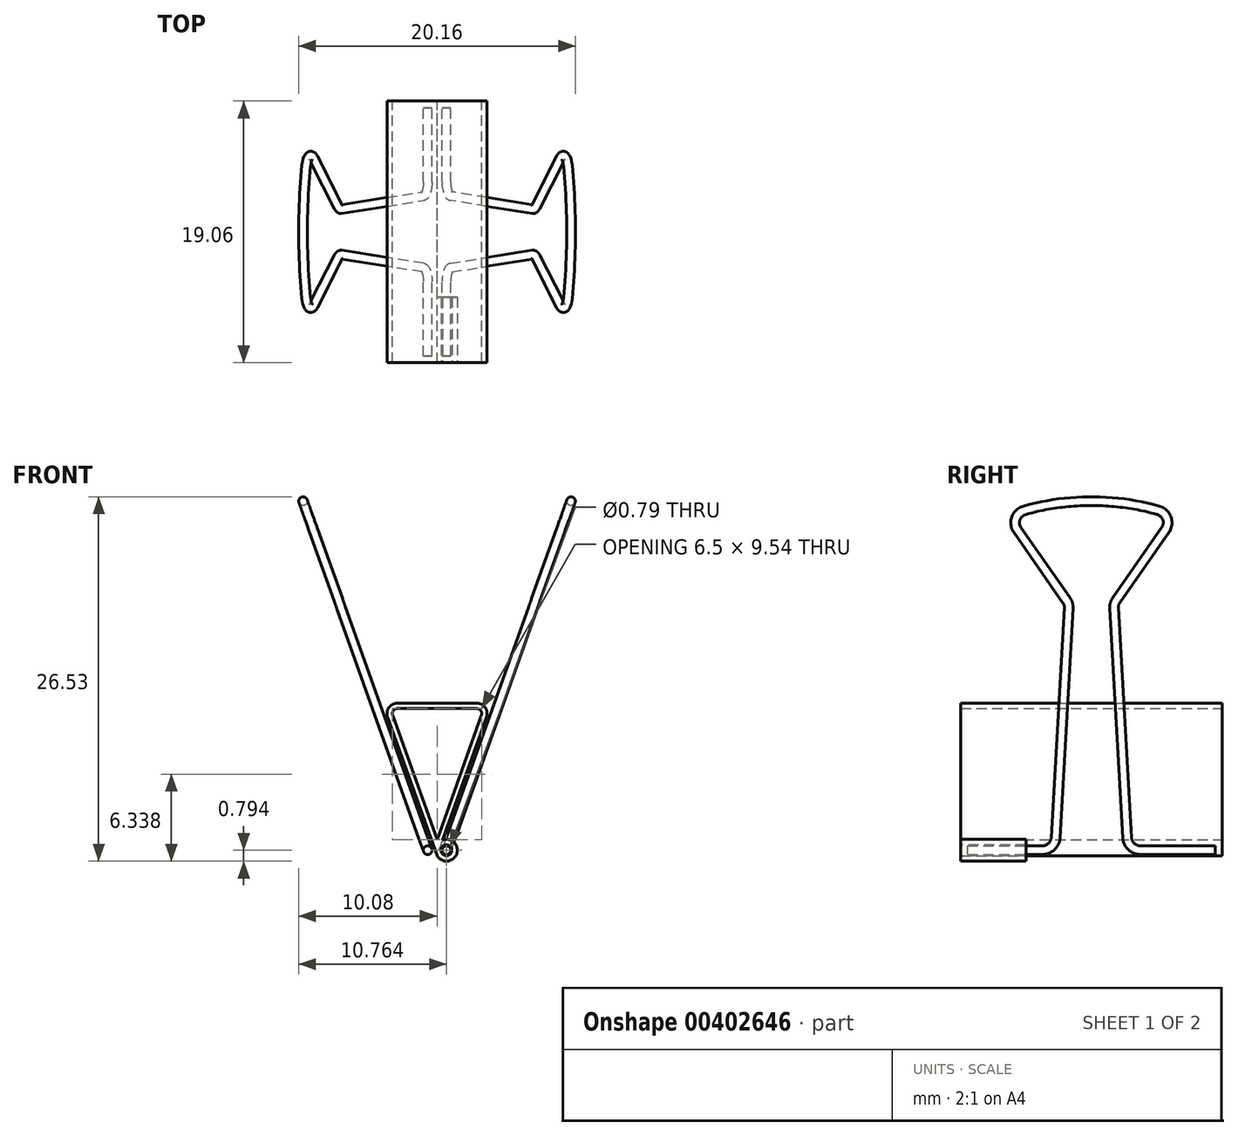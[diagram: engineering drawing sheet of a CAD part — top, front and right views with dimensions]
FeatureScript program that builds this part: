
annotation { "Feature Type Name" : "Feature", "Feature Type Description" : "" }
export const myFeature = defineFeature(function(context is Context, id is Id, definition is map)
    precondition{}
    {
        {
            var Q0;
            Q0=qCreatedBy(makeId("Front.planeOp"),FACE);
            var sketch = newSketch(context, id + "F0", { "sketchPlane" : qUnion([Q0])});
            skLineSegment(sketch, "E0", {"start": v(0, 0) * mm, "end": v(-3.97, 11.11) * mm});
            skLineSegment(sketch, "E1", {"start": v(-3.97, 11.11) * mm, "end": v(3.97, 11.11) * mm});
            skLineSegment(sketch, "E2", {"start": v(3.97, 11.11) * mm, "end": v(0, 0) * mm});
            skSolve(sketch);
        }
        {
            var Q0;
            Q0 = qSketchRegion(id + "F0", true);
            extrude(context, id + "F1", {"entities" : qUnion([Q0]), "depth" : 19.05 * mm, "symmetric" : true});
        }
        {
            var Q0;
            Q0=makeQuery(id+"F1.opExtrude","SWEPT_EDGE",EDGE,{"disambiguationData":[OSD([sQuery(id+"F0.wireOp",EDGE,"E1"),sQuery(id+"F0.wireOp",EDGE,"E2")])]});
            var Q1;
            Q1=makeQuery(id+"F1.opExtrude","SWEPT_EDGE",EDGE,{"disambiguationData":[OSD([sQuery(id+"F0.wireOp",EDGE,"E0"),sQuery(id+"F0.wireOp",EDGE,"E1")])]});
            fillet(context, id + "F2", {"entities" : qUnion([Q0, Q1]), "radius" : 0.76 * mm, "tangentPropagation" : true, "allowEdgeOverflow" : false});
        }
        {
            var Q0;
            Q0=makeQuery(id+"F1.opExtrude","CAP_FACE",FACE,{"disambiguationData":[OSD([sQuery(id+"F0.wireOp",EDGE,"E0"),sQuery(id+"F0.wireOp",EDGE,"E1"),sQuery(id+"F0.wireOp",EDGE,"E2")])],"isStart":false});
            shell(context, id + "F3", {"entities" : qUnion([Q0]), "thickness" : 0.4 * mm});
        }
        {
            var Q0;
            Q0=makeQuery(id+"F1.opExtrude","CAP_FACE",FACE,{"disambiguationData":[OSD([sQuery(id+"F0.wireOp",EDGE,"E0"),sQuery(id+"F0.wireOp",EDGE,"E1"),sQuery(id+"F0.wireOp",EDGE,"E2")])],"isStart":true});
            var sketch = newSketch(context, id + "F4", { "sketchPlane" : qUnion([Q0])});
            skLineSegment(sketch, "E3.0", {"start": v(2.89, 10.72) * mm, "end": v(-2.89, 10.72) * mm});
            skArc(sketch, "E4.0", {"start": v(-2.89, 10.72) * mm, "mid": v(-3.19, 10.56) * mm, "end": v(-3.23, 10.23) * mm});
            skLineSegment(sketch, "E5.0", {"start": v(-3.23, 10.23) * mm, "end": v(0, 1.18) * mm});
            skLineSegment(sketch, "E6.0", {"start": v(0, 1.18) * mm, "end": v(3.23, 10.23) * mm});
            skArc(sketch, "E7.0", {"start": v(3.23, 10.23) * mm, "mid": v(3.19, 10.56) * mm, "end": v(2.89, 10.72) * mm});
            skSolve(sketch);
        }
        {
            var Q0;
            Q0 = qSketchRegion(id + "F4", true);
            extrude(context, id + "F5", {"entities" : qUnion([Q0]), "operationType" : NewBodyOperationType.REMOVE, "endBound" : BoundingType.THROUGH_ALL, "oppositeDirection" : true, "depth" : 25.4 * mm});
        }
        {
            var Q0;
            Q0=makeQuery(id+"F1.opExtrude","CAP_FACE",FACE,{"disambiguationData":[OSD([sQuery(id+"F0.wireOp",EDGE,"E0"),sQuery(id+"F0.wireOp",EDGE,"E1"),sQuery(id+"F0.wireOp",EDGE,"E2")])],"isStart":false});
            var sketch = newSketch(context, id + "F6", { "sketchPlane" : qUnion([Q0])});
            skArc(sketch, "E8", {"start": v(0, 0) * mm, "mid": v(1.43, 0.14) * mm, "end": v(0.41, 1.15) * mm});
            skLineSegment(sketch, "E9", {"start": v(0.41, 1.15) * mm, "end": v(0, 0) * mm});
            skSolve(sketch);
        }
        {
            var Q0;
            Q0 = qSketchRegion(id + "F6", true);
            var Q1;
            Q1=makeQuery(id+"F1.opExtrude","CAP_FACE",FACE,{"disambiguationData":[OSD([sQuery(id+"F0.wireOp",EDGE,"E0"),sQuery(id+"F0.wireOp",EDGE,"E1"),sQuery(id+"F0.wireOp",EDGE,"E2")])],"isStart":true});
            extrude(context, id + "F7", {"entities" : qUnion([Q0]), "operationType" : NewBodyOperationType.ADD, "oppositeDirection" : true, "endBoundEntityFace" : qUnion([Q1]), "depth" : 4.76 * mm});
        }
        {
            var Q0;
            Q0=makeQuery(id+"F7.boolean.opBoolean","MERGE",FACE,{"derivedFrom":[makeQuery(id+"F1.opExtrude","CAP_FACE",FACE,{"disambiguationData":[OSD([sQuery(id+"F0.wireOp",EDGE,"E0"),sQuery(id+"F0.wireOp",EDGE,"E1"),sQuery(id+"F0.wireOp",EDGE,"E2")])],"isStart":false}),makeQuery(id+"F7.opExtrude","CAP_FACE",FACE,{"disambiguationData":[OSD([sQuery(id+"F6.wireOp",EDGE,"E8"),sQuery(id+"F6.wireOp",EDGE,"E9")])],"isStart":true})]});
            var sketch = newSketch(context, id + "F8", { "sketchPlane" : qUnion([Q0])});
            skArc(sketch, "E10.0", {"start": v(0, 0) * mm, "mid": v(1.43, 0.14) * mm, "end": v(0.41, 1.15) * mm, "construction": true});
            skCircle(sketch, "E11", {"center": v(0.68, 0.4) * mm, "radius": 0.4 * mm});
            skSolve(sketch);
        }
        {
            var Q0;
            Q0 = qSketchRegion(id + "F8", true);
            extrude(context, id + "F9", {"entities" : qUnion([Q0]), "operationType" : NewBodyOperationType.REMOVE, "endBound" : BoundingType.THROUGH_ALL, "oppositeDirection" : true, "depth" : 25.4 * mm});
        }
        {
            var Q0;
            {var subQ0=sQuery(id+"F6.wireOp",EDGE,"E9");var subQ1=sQuery(id+"F6.wireOp",EDGE,"E8");Q0=makeQuery(id+"F0Y2VeiEara8Gz9_1.1.F7.boolean.opBoolean","MERGE",FACE,{"derivedFrom":[makeQuery(id+"F7.boolean.opBoolean","MERGE",FACE,{"derivedFrom":[makeQuery(id+"F1.opExtrude","CAP_FACE",FACE,{"disambiguationData":[OSD([sQuery(id+"F0.wireOp",EDGE,"E0"),sQuery(id+"F0.wireOp",EDGE,"E1"),sQuery(id+"F0.wireOp",EDGE,"E2")])],"isStart":false}),makeQuery(id+"F7.opExtrude","CAP_FACE",FACE,{"disambiguationData":[OSD([subQ1,subQ0])],"isStart":true})]}),makeQuery(id+"F0Y2VeiEara8Gz9_1.1.F7.opExtrude","CAP_FACE",FACE,{"disambiguationData":[OSD([subQ1,subQ0])],"isStart":true})]});}
            var sketch = newSketch(context, id + "F10", { "sketchPlane" : qUnion([Q0])});
            skCircle(sketch, "E12.0", {"center": v(0.68, 0.4) * mm, "radius": 0.4 * mm, "construction": true});
            skSolve(sketch);
        }
        {
            var Q0;
            Q0=makeQuery(id+"F1.opExtrude","SWEPT_FACE",FACE,{"disambiguationData":[OSD([sQuery(id+"F0.wireOp",EDGE,"E2")])]});
            var Q1;
            Q1=sQuery(id+"F10.wireOp",VERTEX,"E12.0.center");
            cPlane(context, id + "F11", {"entities" : qUnion([Q0, Q1]), "cplaneType" : CPlaneType.PLANE_POINT, "offset" : 0.4 * mm, "width" : 152.4 * mm, "height" : 152.4 * mm});
        }
        {
            var Q0;
            Q0=qCreatedBy(id+"F11.planeOp",FACE);
            var sketch = newSketch(context, id + "F12", { "sketchPlane" : qUnion([Q0])});
            skLineSegment(sketch, "E13.0", {"start": v(-9.53, 0.21) * mm, "end": v(-9.53, 1) * mm, "construction": true});
            skLineSegment(sketch, "E14", {"start": v(-9.03, 0.6) * mm, "end": v(-3.62, 0.6) * mm});
            skPoint(sketch, "E14.startSnap0", {"position": v(-9.53, 0.6) * mm});
            skLineSegment(sketch, "E15", {"start": v(-2.6, 1.57) * mm, "end": v(-1.65, 19.33) * mm});
            skLineSegment(sketch, "E16", {"start": v(-1.82, 19.94) * mm, "end": v(-5.39, 25.37) * mm});
            skArc(sketch, "E17", {"start": v(4.83, 26.9) * mm, "mid": v(0, 27.6) * mm, "end": v(-4.83, 26.9) * mm});
            skLineSegment(sketch, "E18.MirrorCS", {"start": v(1.82, 19.94) * mm, "end": v(5.39, 25.37) * mm});
            skLineSegment(sketch, "E19.MirrorCS", {"start": v(2.6, 1.57) * mm, "end": v(1.65, 19.33) * mm});
            skLineSegment(sketch, "E20.MirrorCS", {"start": v(9.03, 0.6) * mm, "end": v(3.62, 0.6) * mm});
            skPoint(sketch, "E21.visualSharp", {"position": v(-6.11, 26.47) * mm});
            skArc(sketch, "E21.filletArc", {"start": v(-4.83, 26.9) * mm, "mid": v(-5.5, 26.28) * mm, "end": v(-5.39, 25.37) * mm});
            skPoint(sketch, "E22.visualSharp", {"position": v(6.11, 26.47) * mm});
            skArc(sketch, "E22.filletArc", {"start": v(5.39, 25.37) * mm, "mid": v(5.5, 26.28) * mm, "end": v(4.83, 26.9) * mm});
            skPoint(sketch, "E23.visualSharp", {"position": v(1.63, 19.66) * mm});
            skArc(sketch, "E23.filletArc", {"start": v(1.82, 19.94) * mm, "mid": v(1.69, 19.65) * mm, "end": v(1.65, 19.33) * mm});
            skPoint(sketch, "E24.visualSharp", {"position": v(-1.63, 19.66) * mm});
            skArc(sketch, "E24.filletArc", {"start": v(-1.65, 19.33) * mm, "mid": v(-1.69, 19.65) * mm, "end": v(-1.82, 19.94) * mm});
            skPoint(sketch, "E25.visualSharp", {"position": v(-2.66, 0.6) * mm});
            skArc(sketch, "E25.filletArc", {"start": v(-3.62, 0.6) * mm, "mid": v(-2.92, 0.89) * mm, "end": v(-2.6, 1.57) * mm});
            skPoint(sketch, "E26.visualSharp", {"position": v(2.66, 0.6) * mm});
            skArc(sketch, "E26.filletArc", {"start": v(2.6, 1.57) * mm, "mid": v(2.92, 0.89) * mm, "end": v(3.62, 0.6) * mm});
            skSolve(sketch);
        }
        {
            var Q0;
            {var subQ0=sQuery(id+"F6.wireOp",EDGE,"E9");var subQ1=sQuery(id+"F6.wireOp",EDGE,"E8");Q0=makeQuery(id+"F0Y2VeiEara8Gz9_1.1.F7.boolean.opBoolean","MERGE",FACE,{"derivedFrom":[makeQuery(id+"F7.boolean.opBoolean","MERGE",FACE,{"derivedFrom":[makeQuery(id+"F1.opExtrude","CAP_FACE",FACE,{"disambiguationData":[OSD([sQuery(id+"F0.wireOp",EDGE,"E0"),sQuery(id+"F0.wireOp",EDGE,"E1"),sQuery(id+"F0.wireOp",EDGE,"E2")])],"isStart":false}),makeQuery(id+"F7.opExtrude","CAP_FACE",FACE,{"disambiguationData":[OSD([subQ1,subQ0])],"isStart":true})]}),makeQuery(id+"F0Y2VeiEara8Gz9_1.1.F7.opExtrude","CAP_FACE",FACE,{"disambiguationData":[OSD([subQ1,subQ0])],"isStart":true})]});}
            var Q1;
            Q1=sQuery(id+"F12.wireOp",VERTEX,"E14.start");
            cPlane(context, id + "F13", {"entities" : qUnion([Q0, Q1]), "cplaneType" : CPlaneType.PLANE_POINT, "offset" : 25.4 * mm, "width" : 152.4 * mm, "height" : 152.4 * mm});
        }
        {
            var Q0;
            Q0=qCreatedBy(id+"F13.planeOp",FACE);
            var sketch = newSketch(context, id + "F14", { "sketchPlane" : qUnion([Q0])});
            skPoint(sketch, "E27.0", {"position": v(0.68, 0.4) * mm});
            skCircle(sketch, "E28", {"center": v(0.68, 0.4) * mm, "radius": 0.32 * mm});
            skSolve(sketch);
        }
        {
            var Q0;
            Q0 = qSketchRegion(id + "F14", true);
            var Q1;
            Q1 = qConstructionFilter(qBodyType(qCreatedBy(id + "F12" ,EDGE), BodyType.WIRE), ConstructionObject.NO);
            sweep(context, id + "F15", {"profiles" : qUnion([Q0]), "path" : qUnion([Q1])});
        }
        {
            var Q0;
            Q0=makeQuery(id+"F15.opSweep","SWEPT_BODY",BODY,{"disambiguationData":[OSD([sQuery(id+"F12.wireOp",EDGE,"E20.MirrorCS"),sQuery(id+"F14.wireOp",EDGE,"E28")])]});
            var Q1;
            Q1=qCreatedBy(makeId("Right.planeOp"),FACE);
            mirror(context, id + "F16", {"entities" : qUnion([Q0]), "mirrorPlane" : qUnion([Q1])});
        }
    });
